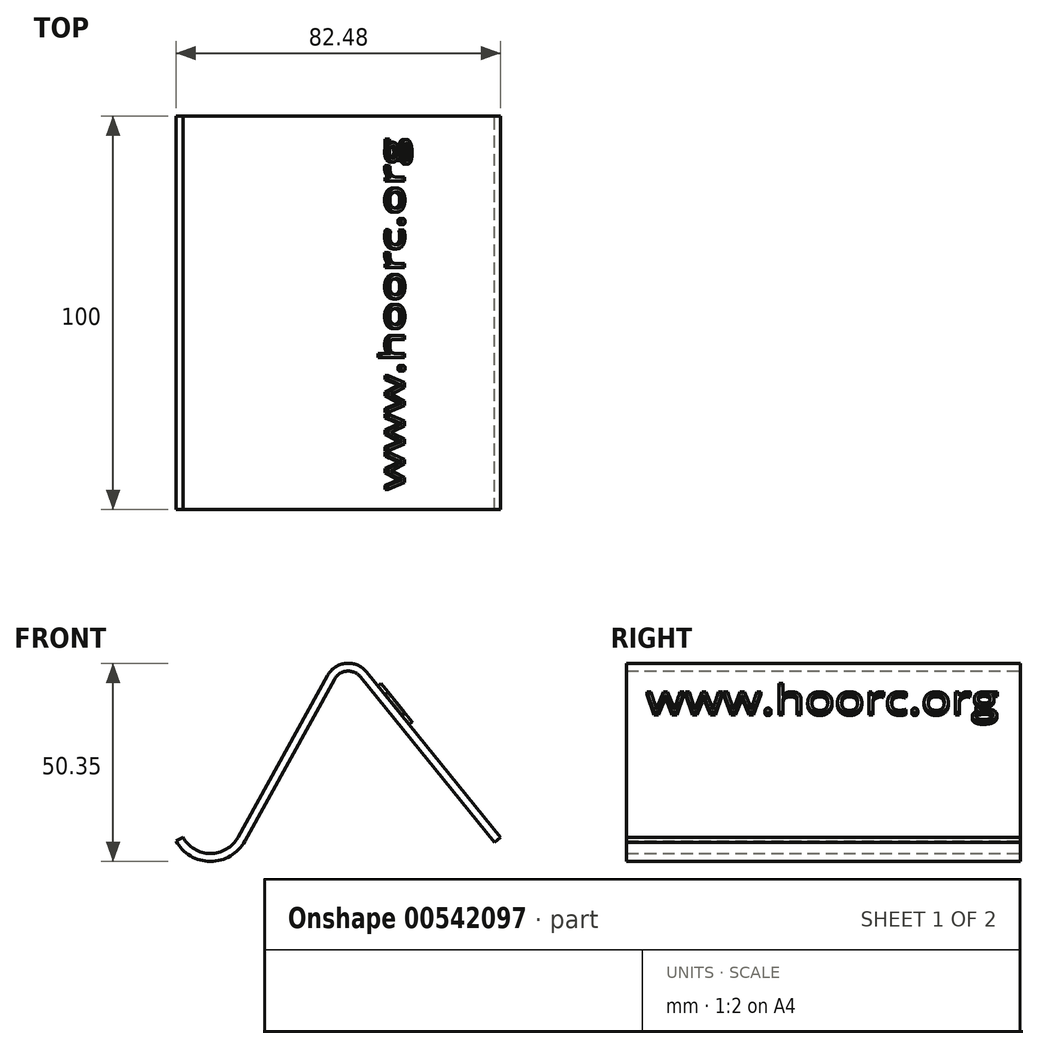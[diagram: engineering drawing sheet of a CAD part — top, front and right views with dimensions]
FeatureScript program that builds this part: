
annotation { "Feature Type Name" : "Feature", "Feature Type Description" : "" }
export const myFeature = defineFeature(function(context is Context, id is Id, definition is map)
    precondition{}
    {
        {
            var Q0;
            Q0=qCreatedBy(makeId("Front.planeOp"),FACE);
            var sketch = newSketch(context, id + "F0", { "sketchPlane" : qUnion([Q0])});
            skLineSegment(sketch, "E0", {"start": v(-27.06, 0) * mm, "end": v(-4.3, 41.13) * mm});
            skLineSegment(sketch, "E1", {"start": v(5.6, 42) * mm, "end": v(39.67, 0) * mm});
            skPoint(sketch, "E2.visualSharp", {"position": v(0, 48.9) * mm});
            skArc(sketch, "E2.filletArc", {"start": v(5.6, 42) * mm, "mid": v(0.42, 44.2) * mm, "end": v(-4.3, 41.13) * mm});
            skArc(sketch, "E3", {"start": v(-41.06, 0) * mm, "mid": v(-34.06, -4.13) * mm, "end": v(-27.06, 0) * mm});
            skLineSegment(sketch, "E4.0", {"start": v(4.05, 40.74) * mm, "end": v(38.12, -1.26) * mm});
            skArc(sketch, "E4.1", {"start": v(4.05, 40.74) * mm, "mid": v(0.6, 42.2) * mm, "end": v(-2.56, 40.16) * mm});
            skLineSegment(sketch, "E4.2", {"start": v(-25.3, -0.97) * mm, "end": v(-2.56, 40.16) * mm});
            skArc(sketch, "E4.3", {"start": v(-42.8, -0.97) * mm, "mid": v(-34.06, -6.13) * mm, "end": v(-25.3, -0.97) * mm});
            skLineSegment(sketch, "E5", {"start": v(-42.8, -0.97) * mm, "end": v(-41.06, 0) * mm});
            skLineSegment(sketch, "E6", {"start": v(38.12, -1.26) * mm, "end": v(39.67, 0) * mm});
            skSolve(sketch);
        }
        {
            var Q0;
            Q0 = qSketchRegion(id + "F0", true);
            extrude(context, id + "F1", {"entities" : qUnion([Q0]), "depth" : 100 * mm, "offsetDistance" : 25 * mm});
        }
        {
            var Q0;
            Q0=makeQuery(id+"F1.opExtrude","SWEPT_FACE",FACE,{"disambiguationData":[OSD([sQuery(id+"F0.wireOp",EDGE,"E1")])]});
            var sketch = newSketch(context, id + "F2", { "sketchPlane" : qUnion([Q0])});
            skText(sketch, "E7", { "text": "www.hoorc.org", "fontName": "OpenSans-Regular.ttf"});
            const initialGuessF2  = {"E7": [-0.095, 0.01497, 1, 0, 0.00903]};
            skSetInitialGuess(sketch, initialGuessF2);
            skSolve(sketch);
        }
        {
            var Q0;
            Q0 = qSketchRegion(id + "F2", true);
            extrude(context, id + "F3", {"entities" : qUnion([Q0]), "operationType" : NewBodyOperationType.ADD, "depth" : 1 * mm, "offsetDistance" : 25 * mm});
        }
    });
